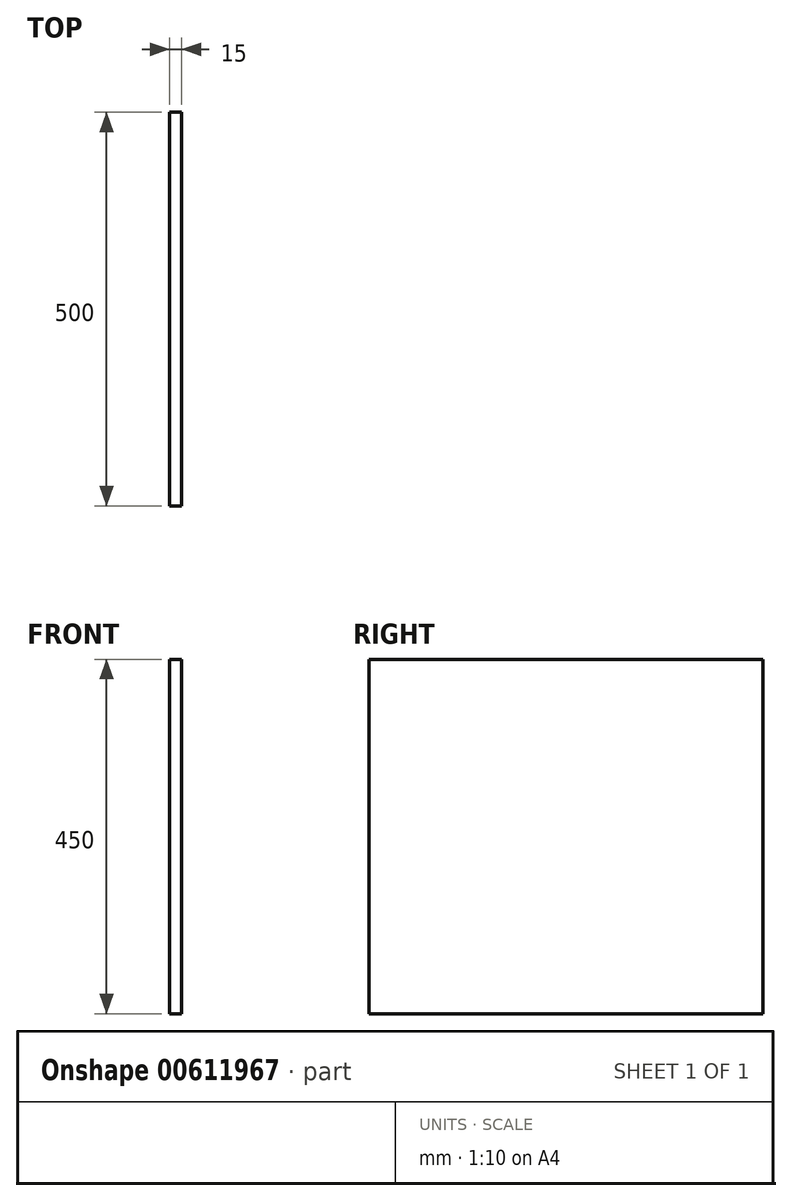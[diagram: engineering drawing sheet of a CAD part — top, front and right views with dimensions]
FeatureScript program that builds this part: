
annotation { "Feature Type Name" : "Feature", "Feature Type Description" : "" }
export const myFeature = defineFeature(function(context is Context, id is Id, definition is map)
    precondition{}
    {
        {
            var Q0;
            Q0=qCreatedBy(makeId("Right.planeOp"),FACE);
            var sketch = newSketch(context, id + "F0", { "sketchPlane" : qUnion([Q0])});
            skLineSegment(sketch, "E0.bottom", {"start": v(-250, 225) * mm, "end": v(250, 225) * mm});
            skLineSegment(sketch, "E0.top", {"start": v(-250, -225) * mm, "end": v(250, -225) * mm});
            skLineSegment(sketch, "E0.left", {"start": v(-250, 225) * mm, "end": v(-250, -225) * mm});
            skLineSegment(sketch, "E0.right", {"start": v(250, 225) * mm, "end": v(250, -225) * mm});
            skPoint(sketch, "E0.middle", {"position": v(0, 0) * mm});
            skSolve(sketch);
        }
        {
            var Q0;
            Q0=qSketchRegion(id+"F0",true);
            extrude(context, id + "F1", {"entities" : qUnion([Q0]), "endBound" : BoundingType.SYMMETRIC, "depth" : 15 * mm, "offsetDistance" : 25 * mm});
        }
    });
